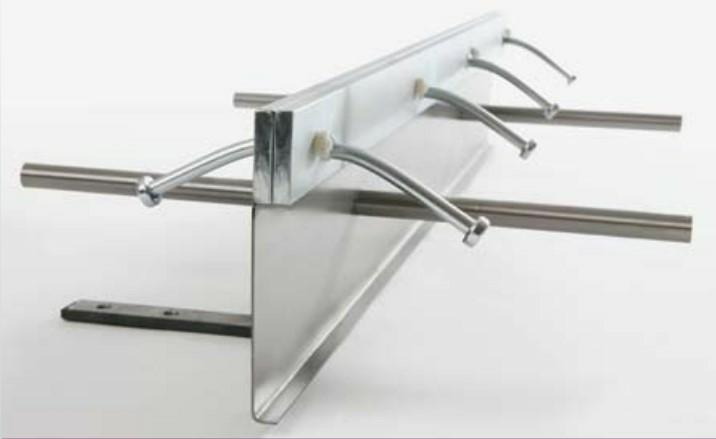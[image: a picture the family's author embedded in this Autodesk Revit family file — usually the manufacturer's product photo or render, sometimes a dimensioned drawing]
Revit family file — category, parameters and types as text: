
# Revit family: Helios SEL_Fugenprofile Dehnfugenprofil Tagesfeldabschalung
name_source: partatom
category: Generic Models
units: mm (PartAtom-declared; Revit-internal decimal feet)

## family parameters
Always vertical = No
Can host rebar = No
Cut with Voids When Loaded = No
Part Type = Normal
Room Calculation Point = No
Round Connector Dimension = Use Diameter
Shared = No
Work Plane-Based = Yes

## types (1)
- HELIOS_SEL_L3000_H500
    Adresse = Iglauer Str. 6 86316 Friedberg
    Default Elevation = 0 mm  [stored 0 ft]
    Description = Schwerlastfugenprofil für industriell genutzte Betonbodenplatten
    Keynote = Helios
    Lieferzeit = 2 weeks
    Manufacturer = Guggemos GmbH
    Model = Schwerlastfugenprofil zur Bauteilentkopplung
    Telefon = +49 (0)8 21 / 455 969 0
    Type Comments = Helios_SEL_L3000
    Type Image = HeliosSel_Foto.jpg
    URL = https://www.fugenprofile.de
    Video = https://www.youtube.com

note: [stored X ft] marks values corroborated as IEEE doubles in the binary element streams (Revit-internal decimal feet)

## geometry (parser evidence)
native form markers: Sweep x14
no freeform markers — native parametric forms only
